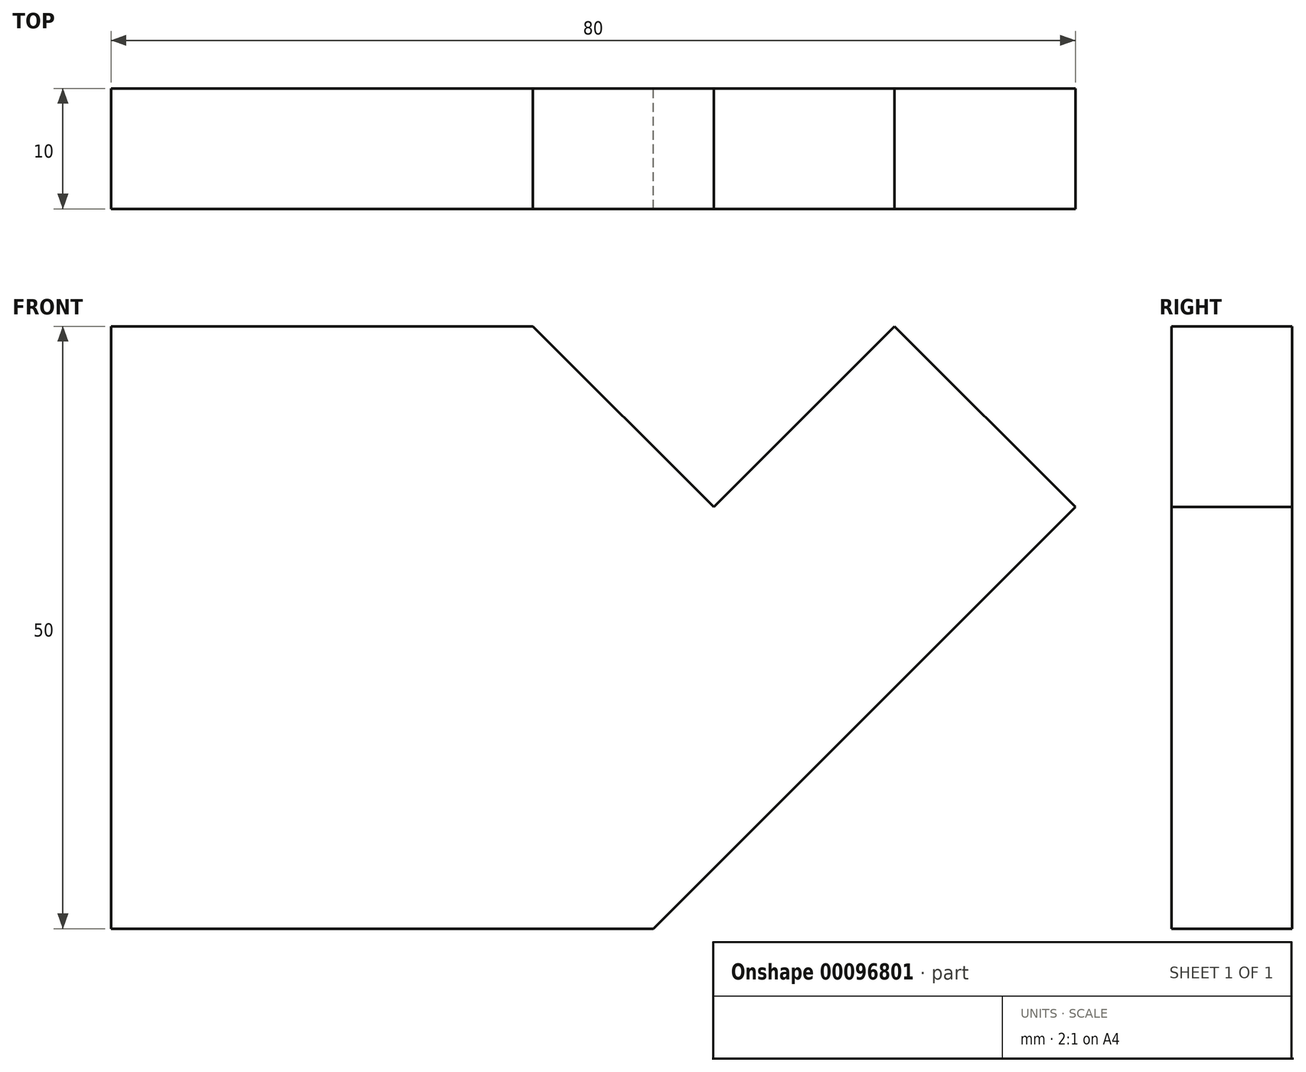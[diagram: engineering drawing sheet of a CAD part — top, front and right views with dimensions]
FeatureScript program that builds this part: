
annotation { "Feature Type Name" : "Feature", "Feature Type Description" : "" }
export const myFeature = defineFeature(function(context is Context, id is Id, definition is map)
    precondition{}
    {
        {
            var Q0;
            Q0=qCreatedBy(makeId("Front.planeOp"),FACE);
            var sketch = newSketch(context, id + "F0", { "sketchPlane" : qUnion([Q0])});
            skLineSegment(sketch, "E0", {"start": v(0, 0) * mm, "end": v(45, 0) * mm});
            skLineSegment(sketch, "E1", {"start": v(45, 0) * mm, "end": v(80, 35) * mm});
            skLineSegment(sketch, "E2", {"start": v(80, 35) * mm, "end": v(65, 50) * mm});
            skLineSegment(sketch, "E3", {"start": v(65, 50) * mm, "end": v(50, 35) * mm});
            skLineSegment(sketch, "E4", {"start": v(50, 35) * mm, "end": v(35, 50) * mm});
            skLineSegment(sketch, "E5", {"start": v(35, 50) * mm, "end": v(0, 50) * mm});
            skLineSegment(sketch, "E6", {"start": v(0, 50) * mm, "end": v(0, 0) * mm});
            skSolve(sketch);
        }
        {
            var Q0;
            Q0 = qSketchRegion(id + "F0", true);
            extrude(context, id + "F1", {"entities" : qUnion([Q0]), "depth" : 10 * mm});
        }
    });
